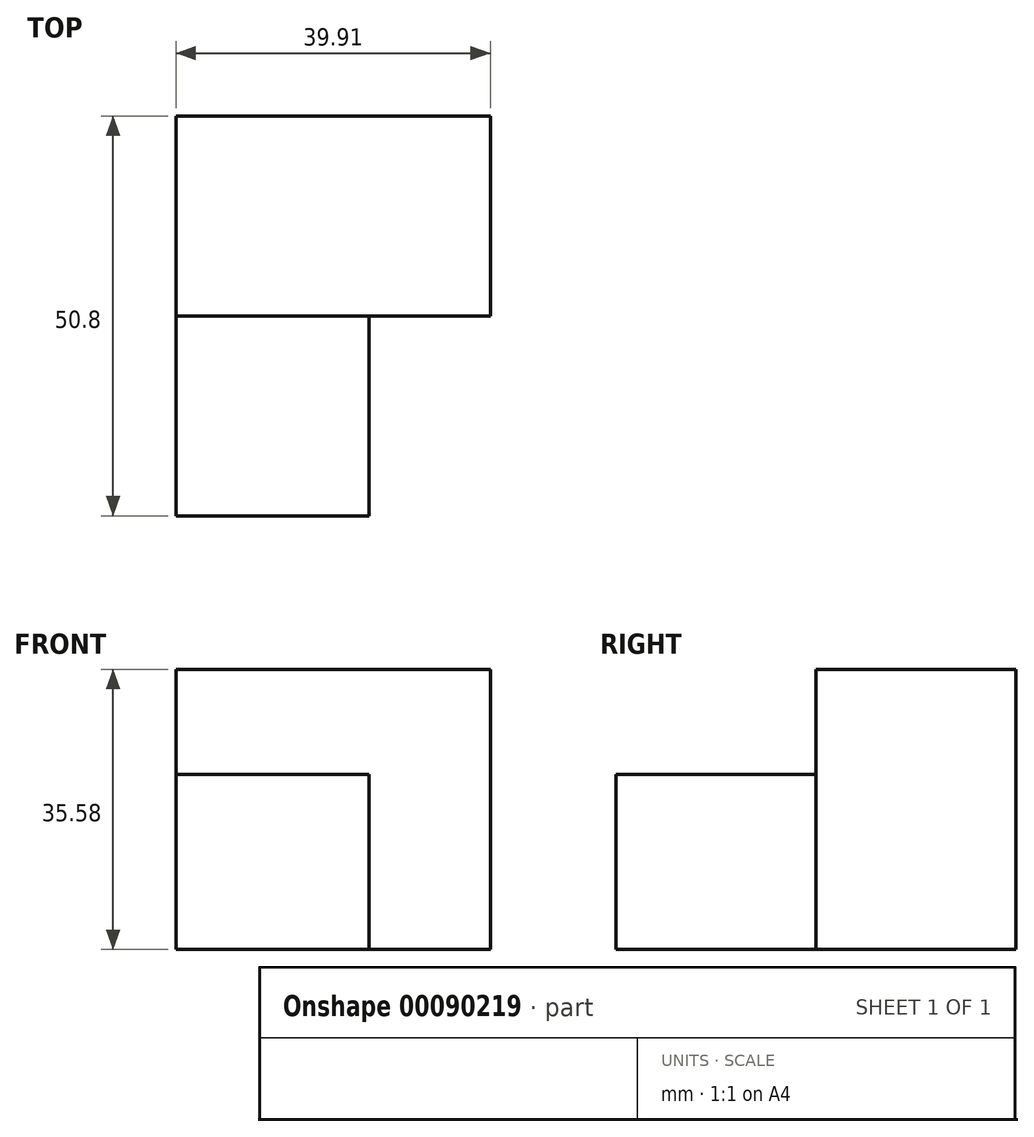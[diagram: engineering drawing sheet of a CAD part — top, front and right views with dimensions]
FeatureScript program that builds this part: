
annotation { "Feature Type Name" : "Feature", "Feature Type Description" : "" }
export const myFeature = defineFeature(function(context is Context, id is Id, definition is map)
    precondition{}
    {
        {
            var Q0;
            Q0=qCreatedBy(makeId("Front.planeOp"),FACE);
            var sketch = newSketch(context, id + "F0", { "sketchPlane" : qUnion([Q0])});
            skLineSegment(sketch, "E0.bottom", {"start": v(0, 0) * mm, "end": v(39.91, 0) * mm});
            skLineSegment(sketch, "E0.top", {"start": v(0, 35.58) * mm, "end": v(39.91, 35.58) * mm});
            skLineSegment(sketch, "E0.left", {"start": v(0, 0) * mm, "end": v(0, 35.58) * mm});
            skLineSegment(sketch, "E0.right", {"start": v(39.91, 0) * mm, "end": v(39.91, 35.58) * mm});
            skSolve(sketch);
        }
        {
            var Q0;
            Q0 = qSketchRegion(id + "F0", true);
            extrude(context, id + "F1", {"entities" : qUnion([Q0]), "depth" : 25.4 * mm, "offsetDistance" : 25.4 * mm});
        }
        {
            var Q0;
            Q0=makeQuery(id+"F1.opExtrude","CAP_FACE",FACE,{"disambiguationData":[OSD([sQuery(id+"F0.wireOp",EDGE,"E0.bottom"),sQuery(id+"F0.wireOp",EDGE,"E0.top"),sQuery(id+"F0.wireOp",EDGE,"E0.left"),sQuery(id+"F0.wireOp",EDGE,"E0.right")])],"isStart":false});
            var sketch = newSketch(context, id + "F2", { "sketchPlane" : qUnion([Q0])});
            skLineSegment(sketch, "E1.bottom", {"start": v(0, 0) * mm, "end": v(24.52, 0) * mm});
            skLineSegment(sketch, "E1.top", {"start": v(0, 22.21) * mm, "end": v(24.52, 22.21) * mm});
            skLineSegment(sketch, "E1.left", {"start": v(0, 0) * mm, "end": v(0, 22.21) * mm});
            skLineSegment(sketch, "E1.right", {"start": v(24.52, 0) * mm, "end": v(24.52, 22.21) * mm});
            skSolve(sketch);
        }
        {
            var Q0;
            Q0 = qSketchRegion(id + "F2", true);
            extrude(context, id + "F3", {"entities" : qUnion([Q0]), "operationType" : NewBodyOperationType.ADD, "depth" : 25.4 * mm, "offsetDistance" : 25.4 * mm});
        }
    });
